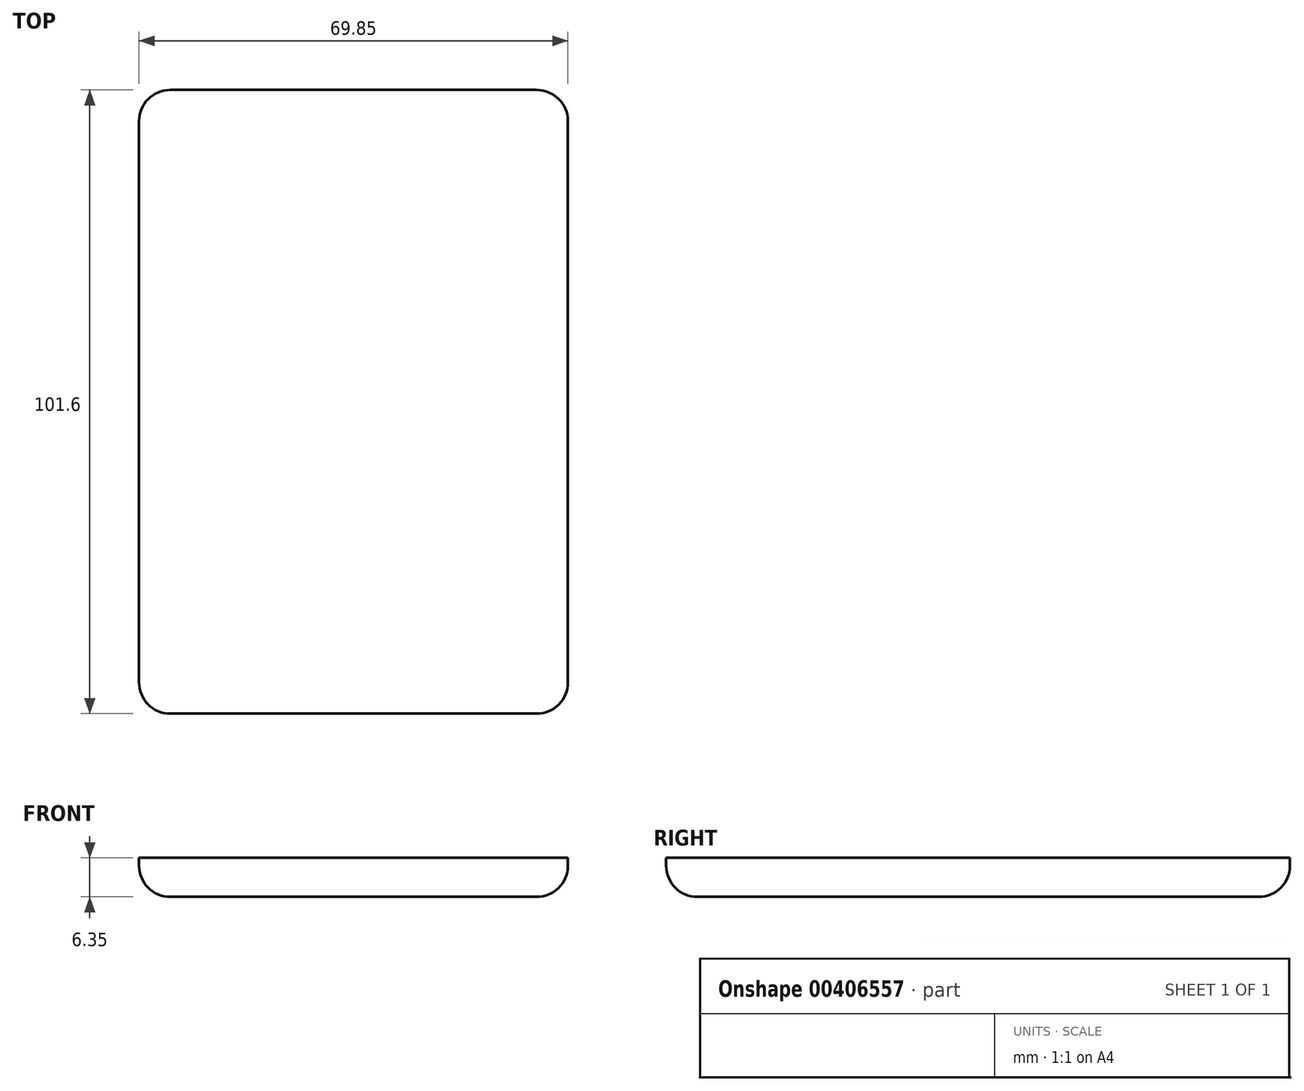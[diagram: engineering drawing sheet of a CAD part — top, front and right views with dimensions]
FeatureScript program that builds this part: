
annotation { "Feature Type Name" : "Feature", "Feature Type Description" : "" }
export const myFeature = defineFeature(function(context is Context, id is Id, definition is map)
    precondition{}
    {
        {
            var Q0;
            Q0=qCreatedBy(makeId("Top.planeOp"),FACE);
            var sketch = newSketch(context, id + "F0", { "sketchPlane" : qUnion([Q0])});
            skLineSegment(sketch, "E0.bottom", {"start": v(0, 0) * mm, "end": v(69.85, 0) * mm});
            skLineSegment(sketch, "E0.top", {"start": v(0, -101.6) * mm, "end": v(69.85, -101.6) * mm});
            skLineSegment(sketch, "E0.left", {"start": v(0, 0) * mm, "end": v(0, -101.6) * mm});
            skLineSegment(sketch, "E0.right", {"start": v(69.85, 0) * mm, "end": v(69.85, -101.6) * mm});
            skSolve(sketch);
        }
        {
            var Q0;
            Q0 = qSketchRegion(id + "F0", true);
            extrude(context, id + "F1", {"entities" : qUnion([Q0]), "depth" : 6.35 * mm});
        }
        {
            var Q0;
            Q0=makeQuery(id+"F1.opExtrude","CAP_EDGE",EDGE,{"disambiguationData":[OSD([sQuery(id+"F0.wireOp",EDGE,"E0.right")])],"isStart":true});
            var Q1;
            Q1=makeQuery(id+"F1.opExtrude","CAP_EDGE",EDGE,{"disambiguationData":[OSD([sQuery(id+"F0.wireOp",EDGE,"E0.top")])],"isStart":true});
            var Q2;
            Q2=makeQuery(id+"F1.opExtrude","CAP_EDGE",EDGE,{"disambiguationData":[OSD([sQuery(id+"F0.wireOp",EDGE,"E0.left")])],"isStart":true});
            var Q3;
            Q3=makeQuery(id+"F1.opExtrude","CAP_EDGE",EDGE,{"disambiguationData":[OSD([sQuery(id+"F0.wireOp",EDGE,"E0.bottom")])],"isStart":true});
            fillet(context, id + "F2", {"entities" : qUnion([Q0, Q1, Q2, Q3]), "radius" : 5.08 * mm, "tangentPropagation" : true, "allowEdgeOverflow" : false});
        }
        {
            var Q0;
            Q0=makeQuery(id+"F1.opExtrude","SWEPT_EDGE",EDGE,{"disambiguationData":[OSD([sQuery(id+"F0.wireOp",EDGE,"E0.top"),sQuery(id+"F0.wireOp",EDGE,"E0.left")])]});
            var Q1;
            Q1=makeQuery(id+"F2.opFillet","BLEND_EDGE",EDGE,{"blendedFrom":[makeQuery(id+"F1.opExtrude","CAP_EDGE",EDGE,{"disambiguationData":[OSD([sQuery(id+"F0.wireOp",EDGE,"E0.top")])],"isStart":true}),makeQuery(id+"F1.opExtrude","CAP_EDGE",EDGE,{"disambiguationData":[OSD([sQuery(id+"F0.wireOp",EDGE,"E0.right")])],"isStart":true})],"blendedInto":[]});
            var Q2;
            Q2=makeQuery(id+"F1.opExtrude","SWEPT_EDGE",EDGE,{"disambiguationData":[OSD([sQuery(id+"F0.wireOp",EDGE,"E0.bottom"),sQuery(id+"F0.wireOp",EDGE,"E0.right")])]});
            var Q3;
            Q3=makeQuery(id+"F1.opExtrude","SWEPT_EDGE",EDGE,{"disambiguationData":[OSD([sQuery(id+"F0.wireOp",EDGE,"E0.bottom"),sQuery(id+"F0.wireOp",EDGE,"E0.left")])]});
            fillet(context, id + "F3", {"entities" : qUnion([Q0, Q1, Q2, Q3]), "radius" : 5.08 * mm, "tangentPropagation" : true, "allowEdgeOverflow" : false});
        }
    });
